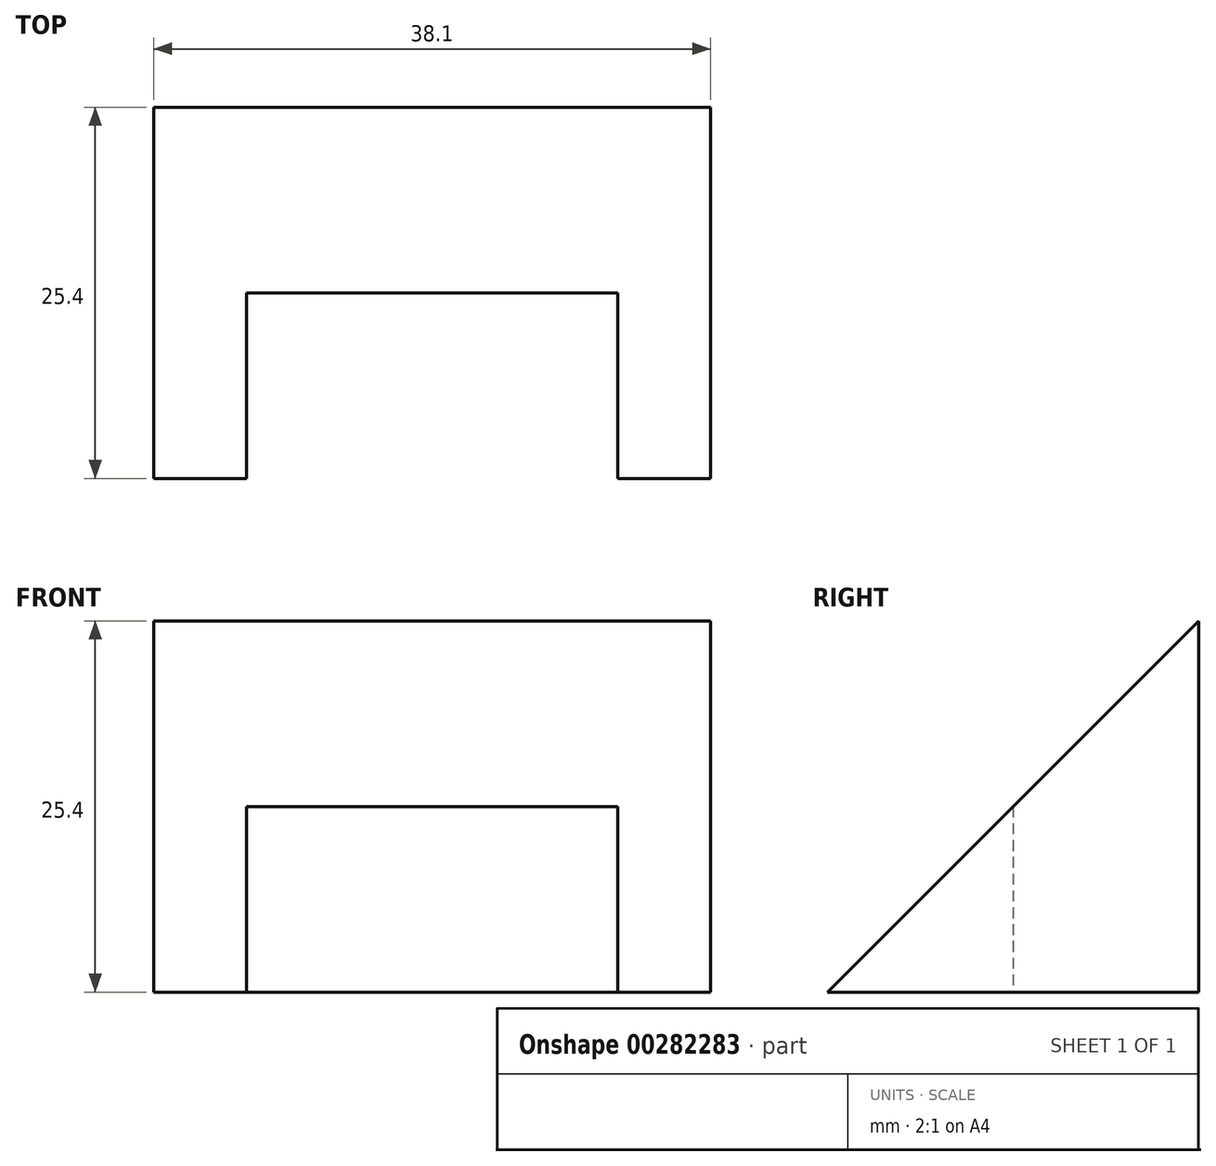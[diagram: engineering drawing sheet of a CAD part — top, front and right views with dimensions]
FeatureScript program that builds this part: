
annotation { "Feature Type Name" : "Feature", "Feature Type Description" : "" }
export const myFeature = defineFeature(function(context is Context, id is Id, definition is map)
    precondition{}
    {
        {
            var Q0;
            Q0=qCreatedBy(makeId("Right.planeOp"),FACE);
            var sketch = newSketch(context, id + "F0", { "sketchPlane" : qUnion([Q0])});
            skLineSegment(sketch, "E0", {"start": v(0, 0) * mm, "end": v(0, 25.4) * mm});
            skLineSegment(sketch, "E1", {"start": v(0, 25.4) * mm, "end": v(-25.4, 0) * mm});
            skLineSegment(sketch, "E2", {"start": v(-25.4, 0) * mm, "end": v(0, 0) * mm});
            skSolve(sketch);
        }
        {
            var Q0;
            Q0 = qSketchRegion(id + "F0", true);
            extrude(context, id + "F1", {"entities" : qUnion([Q0]), "depth" : 38.1 * mm});
        }
        {
            var Q0;
            Q0=makeQuery(id+"F1.opExtrude","SWEPT_FACE",FACE,{"disambiguationData":[OSD([sQuery(id+"F0.wireOp",EDGE,"E2")])]});
            var sketch = newSketch(context, id + "F2", { "sketchPlane" : qUnion([Q0])});
            skLineSegment(sketch, "E3", {"start": v(31.75, 25.4) * mm, "end": v(31.75, 12.7) * mm});
            skLineSegment(sketch, "E4", {"start": v(31.75, 12.7) * mm, "end": v(6.35, 12.7) * mm});
            skLineSegment(sketch, "E5", {"start": v(6.35, 12.7) * mm, "end": v(6.35, 25.4) * mm});
            skLineSegment(sketch, "E6", {"start": v(6.35, 25.4) * mm, "end": v(25.63, 31.69) * mm});
            skLineSegment(sketch, "E7", {"start": v(25.63, 31.69) * mm, "end": v(31.75, 25.4) * mm});
            skSolve(sketch);
        }
        {
            var Q0;
            Q0 = qSketchRegion(id + "F2", true);
            extrude(context, id + "F3", {"entities" : qUnion([Q0]), "operationType" : NewBodyOperationType.REMOVE, "oppositeDirection" : true, "depth" : 25.4 * mm});
        }
    });
